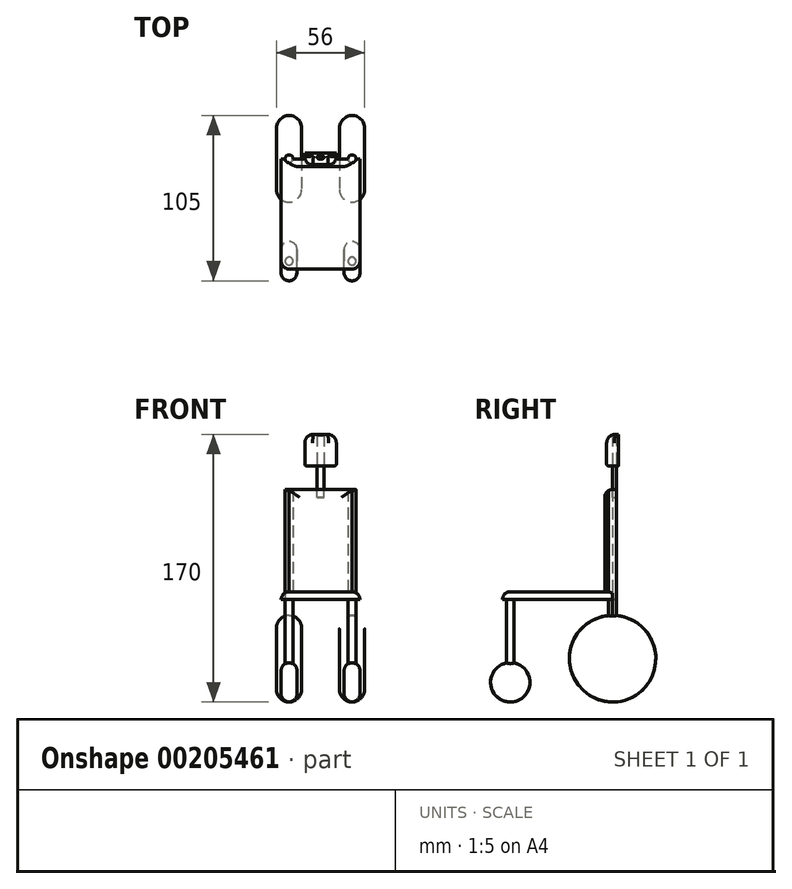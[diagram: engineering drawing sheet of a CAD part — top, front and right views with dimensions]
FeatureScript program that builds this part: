
annotation { "Feature Type Name" : "Feature", "Feature Type Description" : "" }
export const myFeature = defineFeature(function(context is Context, id is Id, definition is map)
    precondition{}
    {
        {
            var Q0;
            Q0=qCreatedBy(makeId("Top.planeOp"),FACE);
            var sketch = newSketch(context, id + "F0", { "sketchPlane" : qUnion([Q0])});
            skLineSegment(sketch, "E0.bottom", {"start": v(-25, 35) * mm, "end": v(25, 35) * mm});
            skLineSegment(sketch, "E0.top", {"start": v(-25, -35) * mm, "end": v(25, -35) * mm});
            skLineSegment(sketch, "E0.left", {"start": v(-25, 35) * mm, "end": v(-25, -35) * mm});
            skLineSegment(sketch, "E0.right", {"start": v(25, 35) * mm, "end": v(25, -35) * mm});
            skPoint(sketch, "E0.middle", {"position": v(0, 0) * mm});
            skSolve(sketch);
        }
        {
            var Q0;
            Q0=makeQuery(id+"F0.imprint","IMPRINT",FACE,{"disambiguationData":[TD([[makeQuery(id+"F0.imprint","IMPRINT",EDGE,{"derivedFrom":sQuery(id+"F0.wireOp",EDGE,"E0.bottom")}),-1.0]])]});
            extrude(context, id + "F1", {"entities" : qUnion([Q0]), "depth" : 5 * mm});
        }
        {
            var Q0;
            Q0=makeQuery(id+"F1.opExtrude","CAP_EDGE",EDGE,{"disambiguationData":[OSD([sQuery(id+"F0.wireOp",EDGE,"E0.top")])],"isStart":false});
            fillet(context, id + "F2", {"entities" : qUnion([Q0]), "radius" : 5 * mm, "tangentPropagation" : true, "allowEdgeOverflow" : false});
        }
        {
            var Q0;
            Q0=makeQuery(id+"F1.opExtrude","CAP_EDGE",EDGE,{"disambiguationData":[OSD([sQuery(id+"F0.wireOp",EDGE,"E0.right")])],"isStart":false});
            fillet(context, id + "F3", {"entities" : qUnion([Q0]), "radius" : 5 * mm, "tangentPropagation" : true, "allowEdgeOverflow" : false});
        }
        {
            var Q0;
            Q0=makeQuery(id+"F1.opExtrude","CAP_EDGE",EDGE,{"disambiguationData":[OSD([sQuery(id+"F0.wireOp",EDGE,"E0.left")])],"isStart":false});
            fillet(context, id + "F4", {"entities" : qUnion([Q0]), "radius" : 5 * mm, "tangentPropagation" : true, "allowEdgeOverflow" : false});
        }
        {
            var Q0;
            Q0=qCreatedBy(makeId("Top.planeOp"),FACE);
            var sketch = newSketch(context, id + "F5", { "sketchPlane" : qUnion([Q0])});
            skCircle(sketch, "E1", {"center": v(-20, 35) * mm, "radius": 2.5 * mm});
            skCircle(sketch, "E2", {"center": v(20, 35) * mm, "radius": 2.5 * mm});
            skSolve(sketch);
        }
        {
            var Q0;
            Q0 = qSketchRegion(id + "F5", true);
            extrude(context, id + "F6", {"entities" : qUnion([Q0]), "operationType" : NewBodyOperationType.ADD, "depth" : 70 * mm});
        }
        {
            var Q0;
            Q0=qCreatedBy(makeId("Top.planeOp"),FACE);
            var sketch = newSketch(context, id + "F7", { "sketchPlane" : qUnion([Q0])});
            skLineSegment(sketch, "E3.bottom", {"start": v(-20, 35) * mm, "end": v(20, 35) * mm});
            skLineSegment(sketch, "E3.top", {"start": v(-20, 30) * mm, "end": v(20, 30) * mm});
            skLineSegment(sketch, "E3.left", {"start": v(-20, 35) * mm, "end": v(-20, 30) * mm});
            skLineSegment(sketch, "E3.right", {"start": v(20, 35) * mm, "end": v(20, 30) * mm});
            skCircle(sketch, "E4.0.0", {"center": v(-20, 35) * mm, "radius": 2.5 * mm});
            skSolve(sketch);
        }
        {
            var Q0;
            Q0 = qSketchRegion(id + "F7", true);
            extrude(context, id + "F8", {"entities" : qUnion([Q0]), "operationType" : NewBodyOperationType.ADD, "depth" : 70 * mm});
        }
        {
            var Q0;
            Q0=makeQuery(id+"F8.opExtrude","SWEPT_EDGE",EDGE,{"disambiguationData":[OSD([sQuery(id+"F7.wireOp",EDGE,"E3.top"),sQuery(id+"F7.wireOp",EDGE,"E3.right")])]});
            var Q1;
            Q1=makeQuery(id+"F8.opExtrude","SWEPT_EDGE",EDGE,{"disambiguationData":[OSD([sQuery(id+"F7.wireOp",EDGE,"E3.top"),sQuery(id+"F7.wireOp",EDGE,"E3.left")])]});
            fillet(context, id + "F9", {"entities" : qUnion([Q0, Q1]), "radius" : 10 * mm, "tangentPropagation" : true, "allowEdgeOverflow" : false});
        }
        {
            var Q0;
            Q0=makeQuery(id+"F8.opExtrude","CAP_EDGE",EDGE,{"disambiguationData":[OSD([sQuery(id+"F7.wireOp",EDGE,"E3.top")])],"isStart":false});
            fillet(context, id + "F10", {"entities" : qUnion([Q0]), "radius" : 5 * mm, "tangentPropagation" : true, "allowEdgeOverflow" : false});
        }
        {
            var Q0;
            Q0=makeQuery(id+"F10.opFillet","SPLIT",FACE,{"disambiguationData":[OD(0.0)],"derivedFrom":makeQuery(id+"F8.boolean.opBoolean","MERGE",FACE,{"derivedFrom":[makeQuery(id+"F6.opExtrude","CAP_FACE",FACE,{"disambiguationData":[OSD([sQuery(id+"F5.wireOp",EDGE,"E1")])],"isStart":false}),makeQuery(id+"F6.opExtrude","CAP_FACE",FACE,{"disambiguationData":[OSD([sQuery(id+"F5.wireOp",EDGE,"E2")])],"isStart":false}),makeQuery(id+"F8.opExtrude","CAP_FACE",FACE,{"disambiguationData":[OSD([sQuery(id+"F7.wireOp",EDGE,"E3.bottom"),sQuery(id+"F7.wireOp",EDGE,"E3.top"),sQuery(id+"F7.wireOp",EDGE,"E3.left"),sQuery(id+"F7.wireOp",EDGE,"E3.right"),sQuery(id+"F7.wireOp",EDGE,"E4.0.0")])],"isStart":false})]})});
            var sketch = newSketch(context, id + "F11", { "sketchPlane" : qUnion([Q0])});
            skPoint(sketch, "E5.0", {"position": v(-20, 35) * mm});
            skPoint(sketch, "E5.1", {"position": v(20, 35) * mm});
            skArc(sketch, "E6", {"start": v(2.5, 35) * mm, "mid": v(0, 37.5) * mm, "end": v(-2.5, 35) * mm});
            skLineSegment(sketch, "E7", {"start": v(-2.5, 35) * mm, "end": v(2.5, 35) * mm});
            skSolve(sketch);
        }
        {
            var Q0;
            Q0 = qSketchRegion(id + "F11", true);
            extrude(context, id + "F12", {"entities" : qUnion([Q0]), "depth" : 15 * mm});
        }
        {
            var Q0;
            {var subQ0=sQuery(id+"F11.wireOp",EDGE,"E7");var subQ1=sQuery(id+"F11.wireOp",EDGE,"E6");Q0=makeQuery(id+"F12.opExtrude","SWEPT_EDGE",EDGE,{"disambiguationData":[OSD([subQ1,subQ0]),TDD([makeQuery(id+"F11.imprint","INTERSECT",VERTEX,{"disambiguationData":[OD(1.0)],"derivedFrom":[subQ1,subQ0]})])]});}
            var Q1;
            {var subQ0=sQuery(id+"F11.wireOp",EDGE,"E7");var subQ1=sQuery(id+"F11.wireOp",EDGE,"E6");Q1=makeQuery(id+"F12.opExtrude","SWEPT_EDGE",EDGE,{"disambiguationData":[OSD([subQ1,subQ0]),TDD([makeQuery(id+"F11.imprint","INTERSECT",VERTEX,{"disambiguationData":[OD(0.0)],"derivedFrom":[subQ1,subQ0]})])]});}
            fillet(context, id + "F13", {"entities" : qUnion([Q0, Q1]), "radius" : 1 * mm, "tangentPropagation" : true, "allowEdgeOverflow" : false});
        }
        {
            var Q0;
            Q0=makeQuery(id+"F12.opExtrude","CAP_FACE",FACE,{"disambiguationData":[OSD([sQuery(id+"F11.wireOp",EDGE,"E6"),sQuery(id+"F11.wireOp",EDGE,"E7")])],"isStart":true});
            extrude(context, id + "F14", {"entities" : qUnion([Q0]), "depth" : 5 * mm});
        }
        {
            var Q0;
            Q0=makeQuery(id+"F12.opExtrude","CAP_FACE",FACE,{"disambiguationData":[OSD([sQuery(id+"F11.wireOp",EDGE,"E6"),sQuery(id+"F11.wireOp",EDGE,"E7")])],"isStart":false});
            var sketch = newSketch(context, id + "F15", { "sketchPlane" : qUnion([Q0])});
            skLineSegment(sketch, "E8.bottom", {"start": v(-10, 31.25) * mm, "end": v(10, 31.25) * mm});
            skLineSegment(sketch, "E8.top", {"start": v(-10, 38.75) * mm, "end": v(10, 38.75) * mm});
            skLineSegment(sketch, "E8.left", {"start": v(-10, 31.25) * mm, "end": v(-10, 38.75) * mm});
            skLineSegment(sketch, "E8.right", {"start": v(10, 31.25) * mm, "end": v(10, 38.75) * mm});
            skPoint(sketch, "E8.middle", {"position": v(0, 35) * mm});
            skSolve(sketch);
        }
        {
            var Q0;
            Q0=makeQuery(id+"F15.imprint","IMPRINT",FACE,{"disambiguationData":[TD([[makeQuery(id+"F15.imprint","IMPRINT",EDGE,{"derivedFrom":sQuery(id+"F15.wireOp",EDGE,"E8.bottom")}),1.0]])]});
            extrude(context, id + "F16", {"entities" : qUnion([Q0]), "operationType" : NewBodyOperationType.ADD, "depth" : 20 * mm});
        }
        {
            var Q0;
            Q0=makeQuery(id+"F16.opExtrude","SWEPT_EDGE",EDGE,{"disambiguationData":[OSD([sQuery(id+"F15.wireOp",EDGE,"E8.bottom"),sQuery(id+"F15.wireOp",EDGE,"E8.left")])]});
            var Q1;
            Q1=makeQuery(id+"F16.opExtrude","SWEPT_EDGE",EDGE,{"disambiguationData":[OSD([sQuery(id+"F15.wireOp",EDGE,"E8.bottom"),sQuery(id+"F15.wireOp",EDGE,"E8.right")])]});
            fillet(context, id + "F17", {"entities" : qUnion([Q0, Q1]), "radius" : 5 * mm, "tangentPropagation" : true, "allowEdgeOverflow" : false});
        }
        {
            var Q0;
            Q0=makeQuery(id+"F16.opExtrude","CAP_EDGE",EDGE,{"disambiguationData":[OSD([sQuery(id+"F15.wireOp",EDGE,"E8.left")])],"isStart":false});
            var Q1;
            {var subQ0=sQuery(id+"F15.wireOp",EDGE,"E8.left");var subQ1=sQuery(id+"F15.wireOp",EDGE,"E8.bottom");Q1=makeQuery(id+"F17.opFillet","BLEND_EDGE",EDGE,{"blendedFrom":[makeQuery(id+"F16.opExtrude","SWEPT_EDGE",EDGE,{"disambiguationData":[OSD([subQ1,subQ0])]}),makeQuery(id+"F16.opExtrude","CAP_FACE",FACE,{"disambiguationData":[OSD([sQuery(id+"F11.wireOp",EDGE,"E6"),sQuery(id+"F11.wireOp",EDGE,"E7"),subQ1,sQuery(id+"F15.wireOp",EDGE,"E8.top"),subQ0,sQuery(id+"F15.wireOp",EDGE,"E8.right")])],"isStart":false})],"blendedInto":[makeQuery(id+"F16.opExtrude","CAP_FACE",FACE,{"disambiguationData":[OSD([sQuery(id+"F11.wireOp",EDGE,"E6"),sQuery(id+"F11.wireOp",EDGE,"E7"),subQ1,sQuery(id+"F15.wireOp",EDGE,"E8.top"),subQ0,sQuery(id+"F15.wireOp",EDGE,"E8.right")])],"isStart":false})]});}
            var Q2;
            Q2=makeQuery(id+"F16.opExtrude","CAP_EDGE",EDGE,{"disambiguationData":[OSD([sQuery(id+"F15.wireOp",EDGE,"E8.bottom")])],"isStart":false});
            var Q3;
            {var subQ0=sQuery(id+"F15.wireOp",EDGE,"E8.right");var subQ1=sQuery(id+"F15.wireOp",EDGE,"E8.bottom");Q3=makeQuery(id+"F17.opFillet","BLEND_EDGE",EDGE,{"blendedFrom":[makeQuery(id+"F16.opExtrude","SWEPT_EDGE",EDGE,{"disambiguationData":[OSD([subQ1,subQ0])]}),makeQuery(id+"F16.opExtrude","CAP_FACE",FACE,{"disambiguationData":[OSD([sQuery(id+"F11.wireOp",EDGE,"E6"),sQuery(id+"F11.wireOp",EDGE,"E7"),subQ1,sQuery(id+"F15.wireOp",EDGE,"E8.top"),sQuery(id+"F15.wireOp",EDGE,"E8.left"),subQ0])],"isStart":false})],"blendedInto":[makeQuery(id+"F16.opExtrude","CAP_FACE",FACE,{"disambiguationData":[OSD([sQuery(id+"F11.wireOp",EDGE,"E6"),sQuery(id+"F11.wireOp",EDGE,"E7"),subQ1,sQuery(id+"F15.wireOp",EDGE,"E8.top"),sQuery(id+"F15.wireOp",EDGE,"E8.left"),subQ0])],"isStart":false})]});}
            var Q4;
            Q4=makeQuery(id+"F16.opExtrude","CAP_EDGE",EDGE,{"disambiguationData":[OSD([sQuery(id+"F15.wireOp",EDGE,"E8.right")])],"isStart":false});
            fillet(context, id + "F18", {"entities" : qUnion([Q0, Q1, Q2, Q3, Q4]), "radius" : 5.5 * mm, "tangentPropagation" : true, "allowEdgeOverflow" : false});
        }
        {
            var Q0;
            Q0=makeQuery(id+"F16.opExtrude","CAP_EDGE",EDGE,{"disambiguationData":[OSD([sQuery(id+"F15.wireOp",EDGE,"E8.bottom")])],"isStart":true});
            var Q1;
            {var subQ0=sQuery(id+"F15.wireOp",EDGE,"E8.right");var subQ1=sQuery(id+"F15.wireOp",EDGE,"E8.bottom");Q1=makeQuery(id+"F17.opFillet","BLEND_EDGE",EDGE,{"blendedFrom":[makeQuery(id+"F16.opExtrude","SWEPT_EDGE",EDGE,{"disambiguationData":[OSD([subQ1,subQ0])]}),makeQuery(id+"F16.opExtrude","CAP_FACE",FACE,{"disambiguationData":[OSD([sQuery(id+"F11.wireOp",EDGE,"E6"),sQuery(id+"F11.wireOp",EDGE,"E7"),subQ1,sQuery(id+"F15.wireOp",EDGE,"E8.top"),sQuery(id+"F15.wireOp",EDGE,"E8.left"),subQ0])],"isStart":true})],"blendedInto":[makeQuery(id+"F16.opExtrude","CAP_FACE",FACE,{"disambiguationData":[OSD([sQuery(id+"F11.wireOp",EDGE,"E6"),sQuery(id+"F11.wireOp",EDGE,"E7"),subQ1,sQuery(id+"F15.wireOp",EDGE,"E8.top"),sQuery(id+"F15.wireOp",EDGE,"E8.left"),subQ0])],"isStart":true})]});}
            var Q2;
            {var subQ0=sQuery(id+"F15.wireOp",EDGE,"E8.left");var subQ1=sQuery(id+"F15.wireOp",EDGE,"E8.bottom");Q2=makeQuery(id+"F17.opFillet","BLEND_EDGE",EDGE,{"blendedFrom":[makeQuery(id+"F16.opExtrude","SWEPT_EDGE",EDGE,{"disambiguationData":[OSD([subQ1,subQ0])]}),makeQuery(id+"F16.opExtrude","CAP_FACE",FACE,{"disambiguationData":[OSD([sQuery(id+"F11.wireOp",EDGE,"E6"),sQuery(id+"F11.wireOp",EDGE,"E7"),subQ1,sQuery(id+"F15.wireOp",EDGE,"E8.top"),subQ0,sQuery(id+"F15.wireOp",EDGE,"E8.right")])],"isStart":true})],"blendedInto":[makeQuery(id+"F16.opExtrude","CAP_FACE",FACE,{"disambiguationData":[OSD([sQuery(id+"F11.wireOp",EDGE,"E6"),sQuery(id+"F11.wireOp",EDGE,"E7"),subQ1,sQuery(id+"F15.wireOp",EDGE,"E8.top"),subQ0,sQuery(id+"F15.wireOp",EDGE,"E8.right")])],"isStart":true})]});}
            fillet(context, id + "F19", {"entities" : qUnion([Q0, Q1, Q2]), "radius" : 1 * mm, "tangentPropagation" : true, "allowEdgeOverflow" : false});
        }
        {
            var Q0;
            Q0=makeQuery(id+"F6.boolean.opBoolean","MERGE",FACE,{"derivedFrom":[makeQuery(id+"F1.opExtrude","CAP_FACE",FACE,{"disambiguationData":[OSD([sQuery(id+"F0.wireOp",EDGE,"E0.bottom"),sQuery(id+"F0.wireOp",EDGE,"E0.top"),sQuery(id+"F0.wireOp",EDGE,"E0.left"),sQuery(id+"F0.wireOp",EDGE,"E0.right")])],"isStart":true}),makeQuery(id+"F6.opExtrude","CAP_FACE",FACE,{"disambiguationData":[OSD([sQuery(id+"F5.wireOp",EDGE,"E1")])],"isStart":true}),makeQuery(id+"F6.opExtrude","CAP_FACE",FACE,{"disambiguationData":[OSD([sQuery(id+"F5.wireOp",EDGE,"E2")])],"isStart":true})]});
            var sketch = newSketch(context, id + "F20", { "sketchPlane" : qUnion([Q0])});
            skCircle(sketch, "E9", {"center": v(-20, 30) * mm, "radius": 2.5 * mm});
            skCircle(sketch, "E10", {"center": v(20, 30) * mm, "radius": 2.5 * mm});
            skSolve(sketch);
        }
        {
            var Q0;
            Q0 = qSketchRegion(id + "F20", true);
            extrude(context, id + "F21", {"entities" : qUnion([Q0]), "operationType" : NewBodyOperationType.ADD, "depth" : 52.5 * mm});
        }
        {
            var Q0;
            Q0=makeQuery(id+"F6.boolean.opBoolean","MERGE",FACE,{"derivedFrom":[makeQuery(id+"F1.opExtrude","CAP_FACE",FACE,{"disambiguationData":[OSD([sQuery(id+"F0.wireOp",EDGE,"E0.bottom"),sQuery(id+"F0.wireOp",EDGE,"E0.top"),sQuery(id+"F0.wireOp",EDGE,"E0.left"),sQuery(id+"F0.wireOp",EDGE,"E0.right")])],"isStart":true}),makeQuery(id+"F6.opExtrude","CAP_FACE",FACE,{"disambiguationData":[OSD([sQuery(id+"F5.wireOp",EDGE,"E1")])],"isStart":true}),makeQuery(id+"F6.opExtrude","CAP_FACE",FACE,{"disambiguationData":[OSD([sQuery(id+"F5.wireOp",EDGE,"E2")])],"isStart":true})]});
            var sketch = newSketch(context, id + "F22", { "sketchPlane" : qUnion([Q0])});
            skLineSegment(sketch, "E11", {"start": v(-20, 30) * mm, "end": v(-20, -35) * mm});
            skLineSegment(sketch, "E12", {"start": v(20, 30) * mm, "end": v(20, -35) * mm});
            skSolve(sketch);
        }
        {
            var Q0;
            {var subQ0=sQuery(id+"F5.wireOp",EDGE,"E1");Q0=makeQuery(id+"F22.imprint","IMPRINT",FACE,{"disambiguationData":[TD([[makeQuery(id+"F22.imprint","IMPRINT",EDGE,{"derivedFrom":makeQuery(id+"F6.opExtrude","CAP_EDGE",EDGE,{"disambiguationData":[OSD([subQ0])],"isStart":true})}),-1.0]])]});}
            var sketch = newSketch(context, id + "F23", { "sketchPlane" : qUnion([Q0])});
            skCircle(sketch, "E13", {"center": v(-20, -35) * mm, "radius": 2.38 * mm});
            skCircle(sketch, "E14", {"center": v(20, -35) * mm, "radius": 2.55 * mm});
            skSolve(sketch);
        }
        {
            var Q0;
            {var subQ7=sQuery(id+"F5.wireOp",EDGE,"E2");var subQ15=makeQuery(id+"F22.imprint","IMPRINT",EDGE,{"derivedFrom":makeQuery(id+"F6.opExtrude","CAP_EDGE",EDGE,{"disambiguationData":[OSD([subQ7])],"isStart":true})});Q0=makeQuery(id+"F23.imprint","IMPRINT",FACE,{"disambiguationData":[TD([[makeQuery(id+"F23.imprint","IMPRINT",EDGE,{"derivedFrom":subQ15}),-1.0]])]});}
            var Q1;
            Q1=makeQuery(id+"F23.imprint","IMPRINT",FACE,{"disambiguationData":[TD([[makeQuery(id+"F23.imprint","IMPRINT",EDGE,{"derivedFrom":sQuery(id+"F23.wireOp",EDGE,"E13")}),1.0]])]});
            extrude(context, id + "F24", {"entities" : qUnion([Q0, Q1]), "operationType" : NewBodyOperationType.ADD, "depth" : 37.5 * mm});
        }
        {
            var Q0;
            Q0=qCreatedBy(makeId("Right.planeOp"),FACE);
            cPlane(context, id + "F25", {"entities" : qUnion([Q0]), "cplaneType" : CPlaneType.OFFSET, "offset" : 20 * mm, "width" : 150 * mm, "height" : 150 * mm});
        }
        {
            var Q0;
            Q0=qCreatedBy(makeId("Right.planeOp"),FACE);
            cPlane(context, id + "F26", {"entities" : qUnion([Q0]), "cplaneType" : CPlaneType.OFFSET, "offset" : 20 * mm, "oppositeDirection" : true, "width" : 150 * mm, "height" : 150 * mm});
        }
        {
            var Q0;
            Q0=makeQuery(id+"F21.opExtrude","CAP_FACE",FACE,{"disambiguationData":[OSD([sQuery(id+"F20.wireOp",EDGE,"E9")])],"isStart":false});
            var sketch = newSketch(context, id + "F27", { "sketchPlane" : qUnion([Q0])});
            skPoint(sketch, "E15", {"position": v(-20, 30) * mm});
            skSolve(sketch);
        }
        {
            var Q0;
            Q0=makeQuery(id+"F21.opExtrude","CAP_FACE",FACE,{"disambiguationData":[OSD([sQuery(id+"F20.wireOp",EDGE,"E10")])],"isStart":false});
            var sketch = newSketch(context, id + "F28", { "sketchPlane" : qUnion([Q0])});
            skPoint(sketch, "E16", {"position": v(20, 30) * mm});
            skSolve(sketch);
        }
        {
            var Q0;
            Q0=qCreatedBy(id+"F26.planeOp",FACE);
            var sketch = newSketch(context, id + "F29", { "sketchPlane" : qUnion([Q0])});
            skCircle(sketch, "E17", {"center": v(-30, -52.5) * mm, "radius": 12.5 * mm});
            skSolve(sketch);
        }
        {
            var Q0;
            Q0 = qSketchRegion(id + "F29", true);
            extrude(context, id + "F30", {"entities" : qUnion([Q0]), "operationType" : NewBodyOperationType.ADD, "depth" : 5 * mm});
        }
        {
            var Q0;
            Q0 = qSketchRegion(id + "F29", true);
            extrude(context, id + "F31", {"entities" : qUnion([Q0]), "operationType" : NewBodyOperationType.ADD, "oppositeDirection" : true, "depth" : 5 * mm});
        }
        {
            var Q0;
            Q0=makeQuery(id+"F30.opExtrude","CAP_EDGE",EDGE,{"disambiguationData":[OSD([sQuery(id+"F29.wireOp",EDGE,"E17")])],"isStart":false});
            var Q1;
            Q1=makeQuery(id+"F31.opExtrude","CAP_EDGE",EDGE,{"disambiguationData":[OSD([sQuery(id+"F29.wireOp",EDGE,"E17")])],"isStart":false});
            fillet(context, id + "F32", {"entities" : qUnion([Q0, Q1]), "radius" : 5 * mm, "tangentPropagation" : true, "allowEdgeOverflow" : false});
        }
        {
            var Q0;
            Q0=qCreatedBy(id+"F25.planeOp",FACE);
            var sketch = newSketch(context, id + "F33", { "sketchPlane" : qUnion([Q0])});
            skCircle(sketch, "E18", {"center": v(-30, -52.5) * mm, "radius": 12.5 * mm});
            skSolve(sketch);
        }
        {
            var Q0;
            Q0 = qSketchRegion(id + "F33", true);
            extrude(context, id + "F34", {"entities" : qUnion([Q0]), "operationType" : NewBodyOperationType.ADD, "depth" : 5 * mm});
        }
        {
            var Q0;
            Q0 = qSketchRegion(id + "F33", true);
            var Q1;
            Q1=makeQuery(id+"F34.opExtrude","CAP_FACE",FACE,{"disambiguationData":[OSD([sQuery(id+"F33.wireOp",EDGE,"E18")])],"isStart":true});
            extrude(context, id + "F35", {"entities" : qUnion([Q0, Q1]), "operationType" : NewBodyOperationType.ADD, "oppositeDirection" : true, "depth" : 5 * mm});
        }
        {
            var Q0;
            {var subQ0=sQuery(id+"F33.wireOp",EDGE,"E18");Q0=makeQuery(id+"F35.opExtrude","CAP_EDGE",EDGE,{"disambiguationData":[OSD([subQ0]),TDD([makeQuery(id+"F33.imprint","IMPRINT",EDGE,{"derivedFrom":subQ0})])],"isStart":false});}
            var Q1;
            Q1=makeQuery(id+"F34.opExtrude","CAP_EDGE",EDGE,{"disambiguationData":[OSD([sQuery(id+"F33.wireOp",EDGE,"E18")])],"isStart":false});
            fillet(context, id + "F36", {"entities" : qUnion([Q0, Q1]), "radius" : 5 * mm, "tangentPropagation" : true, "allowEdgeOverflow" : false});
        }
        {
            var Q0;
            Q0=makeQuery(id+"F24.opExtrude","CAP_FACE",FACE,{"disambiguationData":[OSD([sQuery(id+"F23.wireOp",EDGE,"E13")])],"isStart":false});
            var sketch = newSketch(context, id + "F37", { "sketchPlane" : qUnion([Q0])});
            skPoint(sketch, "E19", {"position": v(-20, -35) * mm});
            skSolve(sketch);
        }
        {
            var Q0;
            Q0=makeQuery(id+"F24.opExtrude","CAP_FACE",FACE,{"disambiguationData":[OSD([sQuery(id+"F0.wireOp",EDGE,"E0.bottom"),sQuery(id+"F5.wireOp",EDGE,"E2"),sQuery(id+"F23.wireOp",EDGE,"E14")])],"isStart":false});
            var sketch = newSketch(context, id + "F38", { "sketchPlane" : qUnion([Q0])});
            skPoint(sketch, "E20", {"position": v(20, -35) * mm});
            skSolve(sketch);
        }
        {
            var Q0;
            Q0=qCreatedBy(id+"F25.planeOp",FACE);
            var sketch = newSketch(context, id + "F39", { "sketchPlane" : qUnion([Q0])});
            skCircle(sketch, "E21", {"center": v(35, -37.5) * mm, "radius": 27.5 * mm});
            skSolve(sketch);
        }
        {
            var Q0;
            Q0 = qSketchRegion(id + "F39", true);
            extrude(context, id + "F40", {"entities" : qUnion([Q0]), "operationType" : NewBodyOperationType.ADD, "depth" : 8 * mm});
        }
        {
            var Q0;
            Q0 = qSketchRegion(id + "F39", true);
            var Q1;
            Q1=makeQuery(id+"F40.opExtrude","CAP_FACE",FACE,{"disambiguationData":[OSD([sQuery(id+"F39.wireOp",EDGE,"E21")])],"isStart":true});
            extrude(context, id + "F41", {"entities" : qUnion([Q0, Q1]), "operationType" : NewBodyOperationType.ADD, "oppositeDirection" : true, "depth" : 8 * mm});
        }
        {
            var Q0;
            {var subQ0=sQuery(id+"F39.wireOp",EDGE,"E21");Q0=makeQuery(id+"F41.opExtrude","CAP_EDGE",EDGE,{"disambiguationData":[OSD([subQ0]),TDD([makeQuery(id+"F39.imprint","IMPRINT",EDGE,{"derivedFrom":subQ0})])],"isStart":false});}
            var Q1;
            Q1=makeQuery(id+"F40.opExtrude","CAP_EDGE",EDGE,{"disambiguationData":[OSD([sQuery(id+"F39.wireOp",EDGE,"E21")])],"isStart":false});
            fillet(context, id + "F42", {"entities" : qUnion([Q0, Q1]), "radius" : 8 * mm, "tangentPropagation" : true, "allowEdgeOverflow" : false});
        }
        {
            var Q0;
            Q0=qCreatedBy(id+"F26.planeOp",FACE);
            var sketch = newSketch(context, id + "F43", { "sketchPlane" : qUnion([Q0])});
            skCircle(sketch, "E22", {"center": v(35, -37.5) * mm, "radius": 27.5 * mm});
            skSolve(sketch);
        }
        {
            var Q0;
            Q0 = qSketchRegion(id + "F43", true);
            extrude(context, id + "F44", {"entities" : qUnion([Q0]), "operationType" : NewBodyOperationType.ADD, "depth" : 8 * mm});
        }
        {
            var Q0;
            Q0 = qSketchRegion(id + "F43", true);
            extrude(context, id + "F45", {"entities" : qUnion([Q0]), "operationType" : NewBodyOperationType.ADD, "oppositeDirection" : true, "depth" : 8 * mm});
        }
        {
            var Q0;
            Q0=makeQuery(id+"F44.opExtrude","CAP_EDGE",EDGE,{"disambiguationData":[OSD([sQuery(id+"F43.wireOp",EDGE,"E22")])],"isStart":false});
            var Q1;
            Q1=makeQuery(id+"F45.opExtrude","CAP_EDGE",EDGE,{"disambiguationData":[OSD([sQuery(id+"F43.wireOp",EDGE,"E22")])],"isStart":false});
            fillet(context, id + "F46", {"entities" : qUnion([Q0, Q1]), "radius" : 8 * mm, "tangentPropagation" : true, "allowEdgeOverflow" : false});
        }
    });
